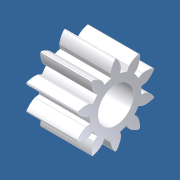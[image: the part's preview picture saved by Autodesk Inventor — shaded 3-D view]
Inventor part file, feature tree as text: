
AUTODESK INVENTOR PART (.ipt)
format: ipt  version: unknown  size: 237,056 bytes
history: native  units: mm
features: other x2, sketch x1
ambient origin geometry x8: Origin, YZ Plane, XZ Plane, XY Plane, X Axis, Y Axis, Z Axis, Center Point
feature tree (3):
  other  "zahnrad_10.ipt"
  other  "Abgeleiteter Körper1"
  sketch  "Skizze1"  dims[d0=10.0mm]
